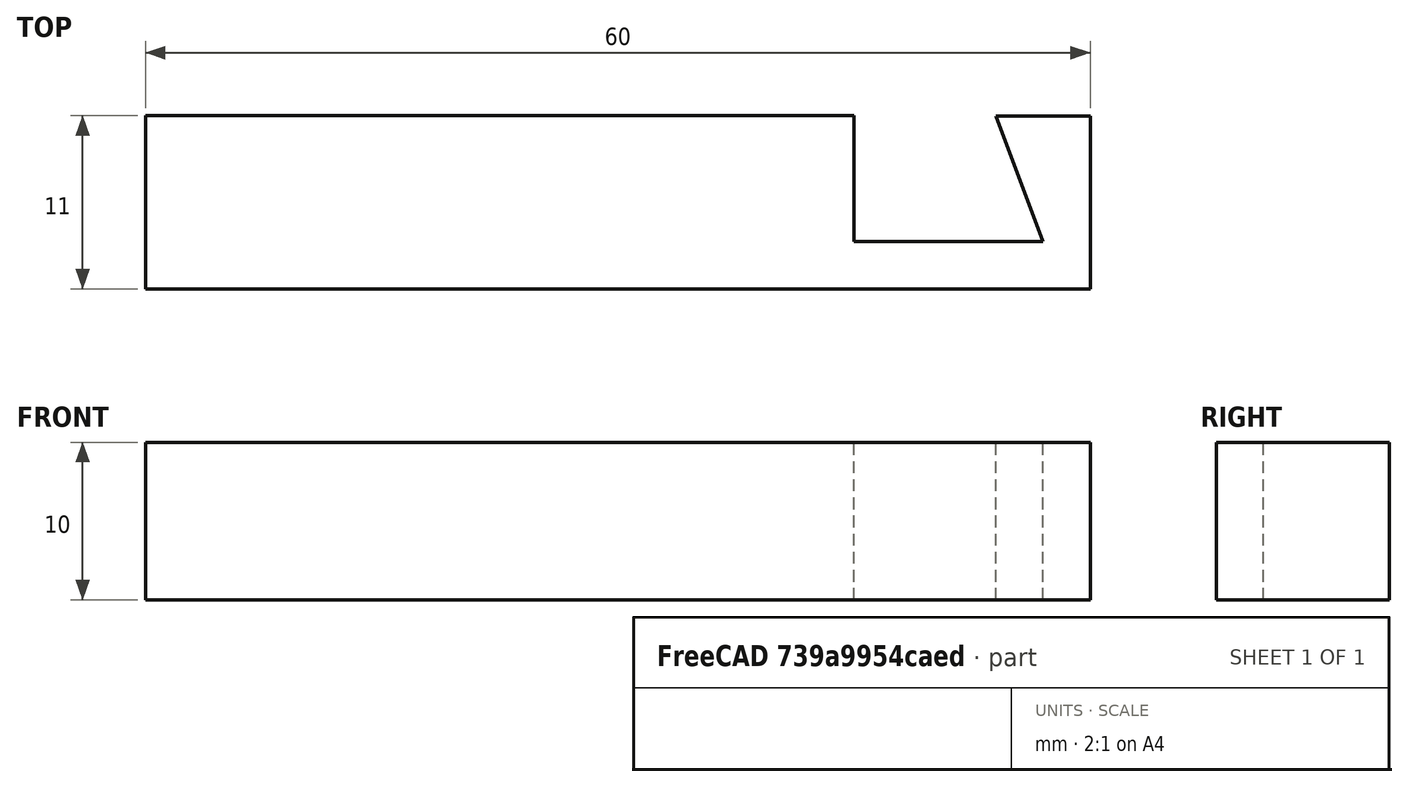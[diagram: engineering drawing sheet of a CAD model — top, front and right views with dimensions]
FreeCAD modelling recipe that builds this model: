
FCSTD DOCUMENT  (FreeCAD 0.20R29410 (Git))
Label: forma_rara_croqueada
License: All rights reserved
LicenseURL: http://en.wikipedia.org/wiki/All_rights_reserved
objects: Sketcher::SketchObject×1, Part::Extrusion×1
note: 2 computed .brp shape members not serialized (recipe doc carries the construction recipe); baked Part::Feature solids carry a one-line shape summary decoded from their .brp

FEATURE [Sketcher::SketchObject] Sketch
  FullyConstrained = false
  sketch-geometry (8):
    g0: LineSegment StartX=0 StartY=0 StartZ=0 EndX=60 EndY=0 EndZ=0
    g1: LineSegment StartX=0 StartY=0 StartZ=0 EndX=0 EndY=11 EndZ=0
    g2: LineSegment StartX=0 StartY=11 StartZ=0 EndX=45 EndY=11 EndZ=0
    g3: LineSegment StartX=45 StartY=11 StartZ=0 EndX=45 EndY=3 EndZ=0
    g4: LineSegment StartX=45 StartY=3 StartZ=0 EndX=57 EndY=3 EndZ=0
    g5: LineSegment StartX=60 StartY=0 StartZ=0 EndX=60 EndY=10.9811 EndZ=0
    g6: LineSegment StartX=60 StartY=10.9811 StartZ=0 EndX=54 EndY=10.9811 EndZ=0
    g7: LineSegment StartX=57 StartY=3 StartZ=0 EndX=54 EndY=10.9811 EndZ=0
  constraints (22):
    c: Horizontal(g0)
    c: Coincident(g0,g-1)
    c: Distance(g0) = 60  'base'
    c: Coincident(g1,g0)
    c: PointOnObject(g1,g-2)
    c: DistanceY(g1,g1) = 11  'altura'
    c: Coincident(g2,g1)
    c: Horizontal(g2)
    c: Coincident(g3,g2)
    c: Vertical(g3)
    c: Coincident(g4,g3)
    c: Horizontal(g4)
    c: Coincident(g5,g0)
    c: Vertical(g5)
    c: DistanceX(g2,g2) = 45
    c: DistanceX(g4,g4) = 12
    c: DistanceY(g3,g3) = 8
    c: Coincident(g6,g5)
    c: Horizontal(g6)
    c: Coincident(g7,g4)
    c: Coincident(g7,g6)
    c: DistanceX(g6,g6) = 6
FEATURE [Part::Extrusion] Extrude
  Base = -> Sketch
  Dir = (0,0,1)
  DirMode = 2
  FaceMakerClass = Part::FaceMakerBullseye
  LengthFwd = 10
  LengthRev = 0
  Solid = true
  Symmetric = false
